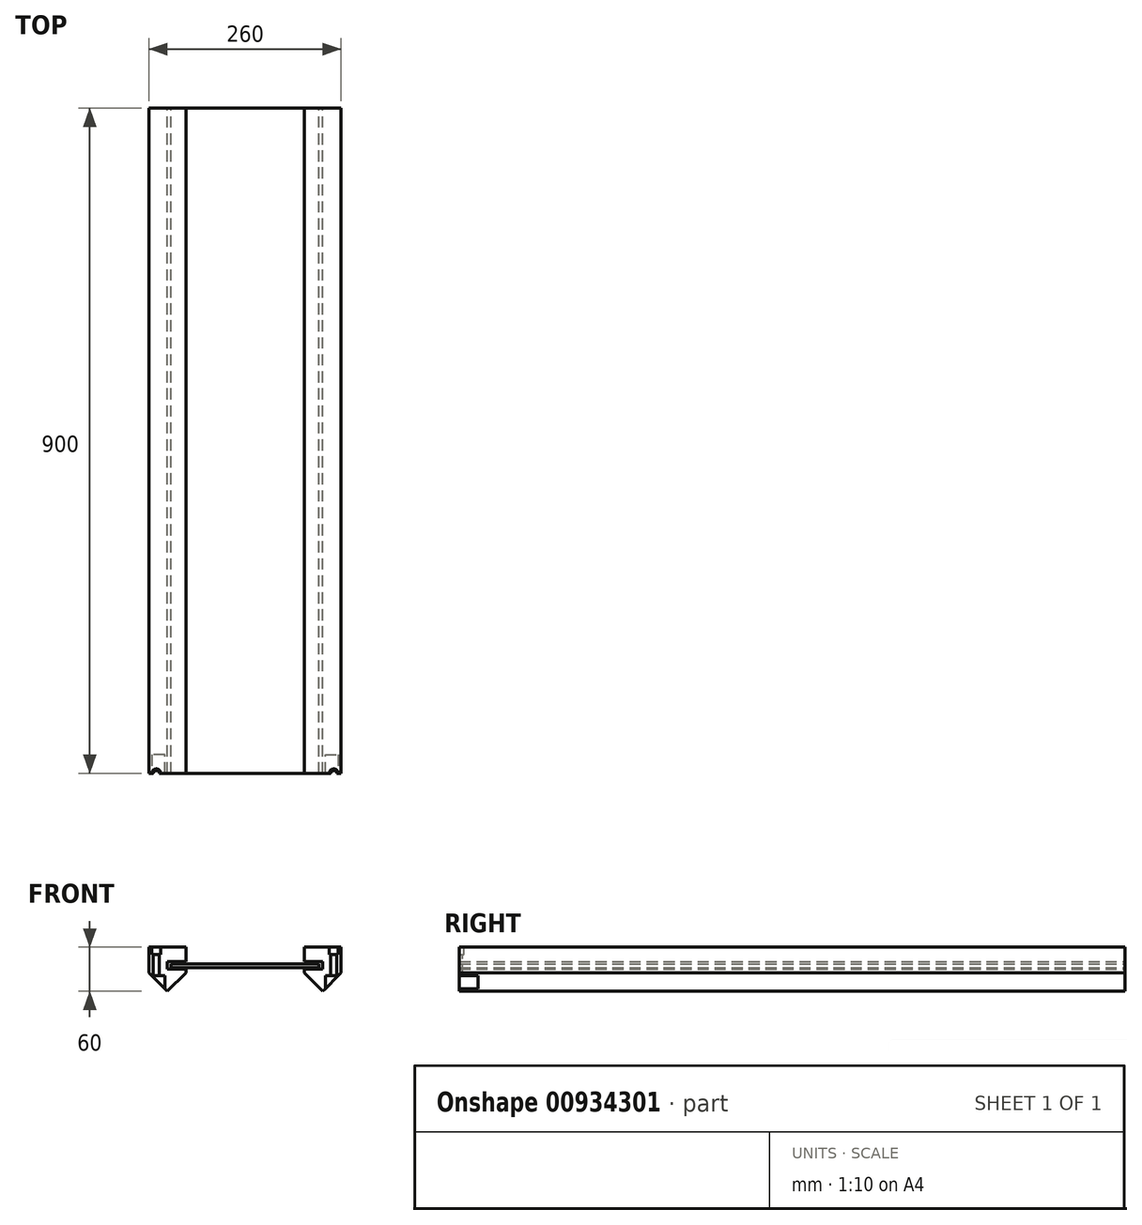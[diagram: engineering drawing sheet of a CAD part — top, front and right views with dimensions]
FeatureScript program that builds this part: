
annotation { "Feature Type Name" : "Feature", "Feature Type Description" : "" }
export const myFeature = defineFeature(function(context is Context, id is Id, definition is map)
    precondition{}
    {
        {
            var Q0;
            Q0=qCreatedBy(makeId("Front.planeOp"),FACE);
            var sketch = newSketch(context, id + "F0", { "sketchPlane" : qUnion([Q0])});
            skLineSegment(sketch, "E0", {"start": v(0, 0) * mm, "end": v(50, 0) * mm});
            skLineSegment(sketch, "E1", {"start": v(50, 0) * mm, "end": v(50, -20) * mm});
            skLineSegment(sketch, "E2", {"start": v(50, -20) * mm, "end": v(25, -20) * mm});
            skLineSegment(sketch, "E3", {"start": v(25, -20) * mm, "end": v(25, -30) * mm});
            skLineSegment(sketch, "E4", {"start": v(25, -30) * mm, "end": v(50, -30) * mm});
            skLineSegment(sketch, "E5", {"start": v(50, -30) * mm, "end": v(50, -35) * mm});
            skLineSegment(sketch, "E6", {"start": v(50, -35) * mm, "end": v(25, -60) * mm});
            skLineSegment(sketch, "E7", {"start": v(25, -60) * mm, "end": v(0, -35) * mm});
            skLineSegment(sketch, "E8", {"start": v(0, -35) * mm, "end": v(0, 0) * mm});
            skSolve(sketch);
        }
        {
            var Q0;
            Q0=makeQuery(id+"F0.imprint","IMPRINT",FACE,{"disambiguationData":[TD([[makeQuery(id+"F0.imprint","IMPRINT",EDGE,{"derivedFrom":sQuery(id+"F0.wireOp",EDGE,"E0")}),-1.0]])]});
            extrude(context, id + "F1", {"entities" : qUnion([Q0]), "endBound" : BoundingType.SYMMETRIC, "depth" : 1000 * mm, "offsetDistance" : 25 * mm});
        }
        {
            var Q0;
            Q0=qCreatedBy(makeId("Front.planeOp"),FACE);
            var sketch = newSketch(context, id + "F2", { "sketchPlane" : qUnion([Q0])});
            skLineSegment(sketch, "E9.bottom", {"start": v(30, -23) * mm, "end": v(130, -23) * mm});
            skLineSegment(sketch, "E9.top", {"start": v(30, -28) * mm, "end": v(130, -28) * mm});
            skLineSegment(sketch, "E9.left", {"start": v(30, -23) * mm, "end": v(30, -28) * mm});
            skLineSegment(sketch, "E9.right", {"start": v(130, -23) * mm, "end": v(130, -28) * mm});
            skSolve(sketch);
        }
        {
            var Q0;
            Q0=makeQuery(id+"F2.imprint","IMPRINT",FACE,{"disambiguationData":[TD([[makeQuery(id+"F2.imprint","IMPRINT",EDGE,{"derivedFrom":sQuery(id+"F2.wireOp",EDGE,"E9.bottom")}),-1.0]])]});
            extrude(context, id + "F3", {"entities" : qUnion([Q0]), "endBound" : BoundingType.SYMMETRIC, "depth" : 1000 * mm, "offsetDistance" : 25 * mm});
        }
        {
            var Q0;
            Q0=qCreatedBy(makeId("Top.planeOp"),FACE);
            var sketch = newSketch(context, id + "F4", { "sketchPlane" : qUnion([Q0])});
            skCircle(sketch, "E10", {"center": v(10, -400) * mm, "radius": 4 * mm});
            skSolve(sketch);
        }
        {
            var Q0;
            Q0=qCreatedBy(makeId("Top.planeOp"),FACE);
            var sketch = newSketch(context, id + "F5", { "sketchPlane" : qUnion([Q0])});
            skCircle(sketch, "E11", {"center": v(10, -400) * mm, "radius": 6 * mm});
            skSolve(sketch);
        }
        {
            var Q0;
            Q0=makeQuery(id+"F4.imprint","IMPRINT",FACE,{"disambiguationData":[TD([[makeQuery(id+"F4.imprint","IMPRINT",EDGE,{"derivedFrom":sQuery(id+"F4.wireOp",EDGE,"E10")}),1.0]])]});
            extrude(context, id + "F6", {"entities" : qUnion([Q0]), "operationType" : NewBodyOperationType.REMOVE, "endBound" : BoundingType.THROUGH_ALL, "oppositeDirection" : true, "depth" : 25 * mm, "offsetDistance" : 25 * mm});
        }
        {
            var Q0;
            Q0=makeQuery(id+"F5.imprint","IMPRINT",FACE,{"disambiguationData":[TD([[makeQuery(id+"F5.imprint","IMPRINT",EDGE,{"derivedFrom":sQuery(id+"F5.wireOp",EDGE,"E11")}),1.0]])]});
            extrude(context, id + "F7", {"entities" : qUnion([Q0]), "operationType" : NewBodyOperationType.REMOVE, "oppositeDirection" : true, "depth" : 10 * mm, "offsetDistance" : 25 * mm});
        }
        {
            var Q0;
            Q0=qCreatedBy(makeId("Top.planeOp"),FACE);
            var sketch = newSketch(context, id + "F8", { "sketchPlane" : qUnion([Q0])});
            skLineSegment(sketch, "E12.bottom", {"start": v(-127.85, -400) * mm, "end": v(250.86, -400) * mm});
            skLineSegment(sketch, "E12.top", {"start": v(-127.85, -531.3) * mm, "end": v(250.86, -531.3) * mm});
            skLineSegment(sketch, "E12.left", {"start": v(-127.85, -400) * mm, "end": v(-127.85, -531.3) * mm});
            skLineSegment(sketch, "E12.right", {"start": v(250.86, -400) * mm, "end": v(250.86, -531.3) * mm});
            skSolve(sketch);
        }
        {
            var Q0;
            Q0=makeQuery(id+"F8.imprint","IMPRINT",FACE,{"disambiguationData":[TD([[makeQuery(id+"F8.imprint","IMPRINT",EDGE,{"derivedFrom":sQuery(id+"F8.wireOp",EDGE,"E12.bottom")}),-1.0]])]});
            extrude(context, id + "F9", {"entities" : qUnion([Q0]), "operationType" : NewBodyOperationType.REMOVE, "endBound" : BoundingType.THROUGH_ALL, "oppositeDirection" : true, "depth" : 25 * mm, "offsetDistance" : 25 * mm, "hasSecondDirection" : true, "secondDirectionBound" : SecondDirectionBoundingType.THROUGH_ALL, "secondDirectionOppositeDirection" : false, "secondDirectionDepth" : 25 * mm});
        }
        {
            var Q0;
            Q0=makeQuery(id+"F9.boolean.opBoolean","COPY",FACE,{"disambiguationData":[TD([makeQuery(id+"F1.opExtrude","SWEPT_FACE",FACE,{"disambiguationData":[OSD([sQuery(id+"F0.wireOp",EDGE,"E1")])]})])],"derivedFrom":makeQuery(id+"F9.opExtrude","SWEPT_FACE",FACE,{"disambiguationData":[OSD([sQuery(id+"F8.wireOp",EDGE,"E12.bottom")])]})});
            var sketch = newSketch(context, id + "F10", { "sketchPlane" : qUnion([Q0])});
            skLineSegment(sketch, "E13.bottom", {"start": v(-6.07, -39.05) * mm, "end": v(21.42, -39.05) * mm});
            skLineSegment(sketch, "E13.top", {"start": v(-6.07, -62.41) * mm, "end": v(21.42, -62.41) * mm});
            skLineSegment(sketch, "E13.left", {"start": v(-6.07, -39.05) * mm, "end": v(-6.07, -62.41) * mm});
            skLineSegment(sketch, "E13.right", {"start": v(21.42, -39.05) * mm, "end": v(21.42, -62.41) * mm});
            skSolve(sketch);
        }
        {
            var Q0;
            {var subQ1=sQuery(id+"F10.wireOp",EDGE,"E13.top");Q0=makeQuery(id+"F10.imprint","IMPRINT",FACE,{"disambiguationData":[TD([[makeQuery(id+"F10.imprint","IMPRINT",EDGE,{"derivedFrom":subQ1}),1.0]])]});}
            var Q1;
            {var subQ0=sQuery(id+"F10.wireOp",EDGE,"E13.right");var subQ1=sQuery(id+"F10.wireOp",EDGE,"E13.bottom");var subQ2=makeQuery(id+"F10.imprint","INTERSECT",VERTEX,{"derivedFrom":[subQ1,subQ0]});Q1=makeQuery(id+"F10.imprint","IMPRINT",FACE,{"disambiguationData":[TD([[makeQuery(id+"F10.imprint","IMPRINT",EDGE,{"disambiguationData":[TD([[subQ2,1.0]])],"derivedFrom":subQ1}),-1.0]])]});}
            extrude(context, id + "F11", {"entities" : qUnion([Q0, Q1]), "operationType" : NewBodyOperationType.REMOVE, "oppositeDirection" : true, "depth" : 25 * mm, "offsetDistance" : 25 * mm});
        }
        {
            var Q0;
            Q0=makeQuery(id+"F1.opExtrude","SWEPT_BODY",BODY,{"disambiguationData":[OSD([sQuery(id+"F0.wireOp",EDGE,"E0"),sQuery(id+"F0.wireOp",EDGE,"E1"),sQuery(id+"F0.wireOp",EDGE,"E2"),sQuery(id+"F0.wireOp",EDGE,"E3"),sQuery(id+"F0.wireOp",EDGE,"E4"),sQuery(id+"F0.wireOp",EDGE,"E5"),sQuery(id+"F0.wireOp",EDGE,"E6"),sQuery(id+"F0.wireOp",EDGE,"E7"),sQuery(id+"F0.wireOp",EDGE,"E8")])]});
            var Q1;
            Q1=makeQuery(id+"F3.opExtrude","SWEPT_BODY",BODY,{"disambiguationData":[OSD([sQuery(id+"F2.wireOp",EDGE,"E9.bottom"),sQuery(id+"F2.wireOp",EDGE,"E9.top"),sQuery(id+"F2.wireOp",EDGE,"E9.left"),sQuery(id+"F2.wireOp",EDGE,"E9.right")])]});
            var Q2;
            Q2=makeQuery(id+"F3.opExtrude","SWEPT_FACE",FACE,{"disambiguationData":[OSD([sQuery(id+"F2.wireOp",EDGE,"E9.right")])]});
            mirror(context, id + "F12", {"operationType" : NewBodyOperationType.ADD, "entities" : qUnion([Q0, Q1]), "mirrorPlane" : qUnion([Q2])});
        }
    });
